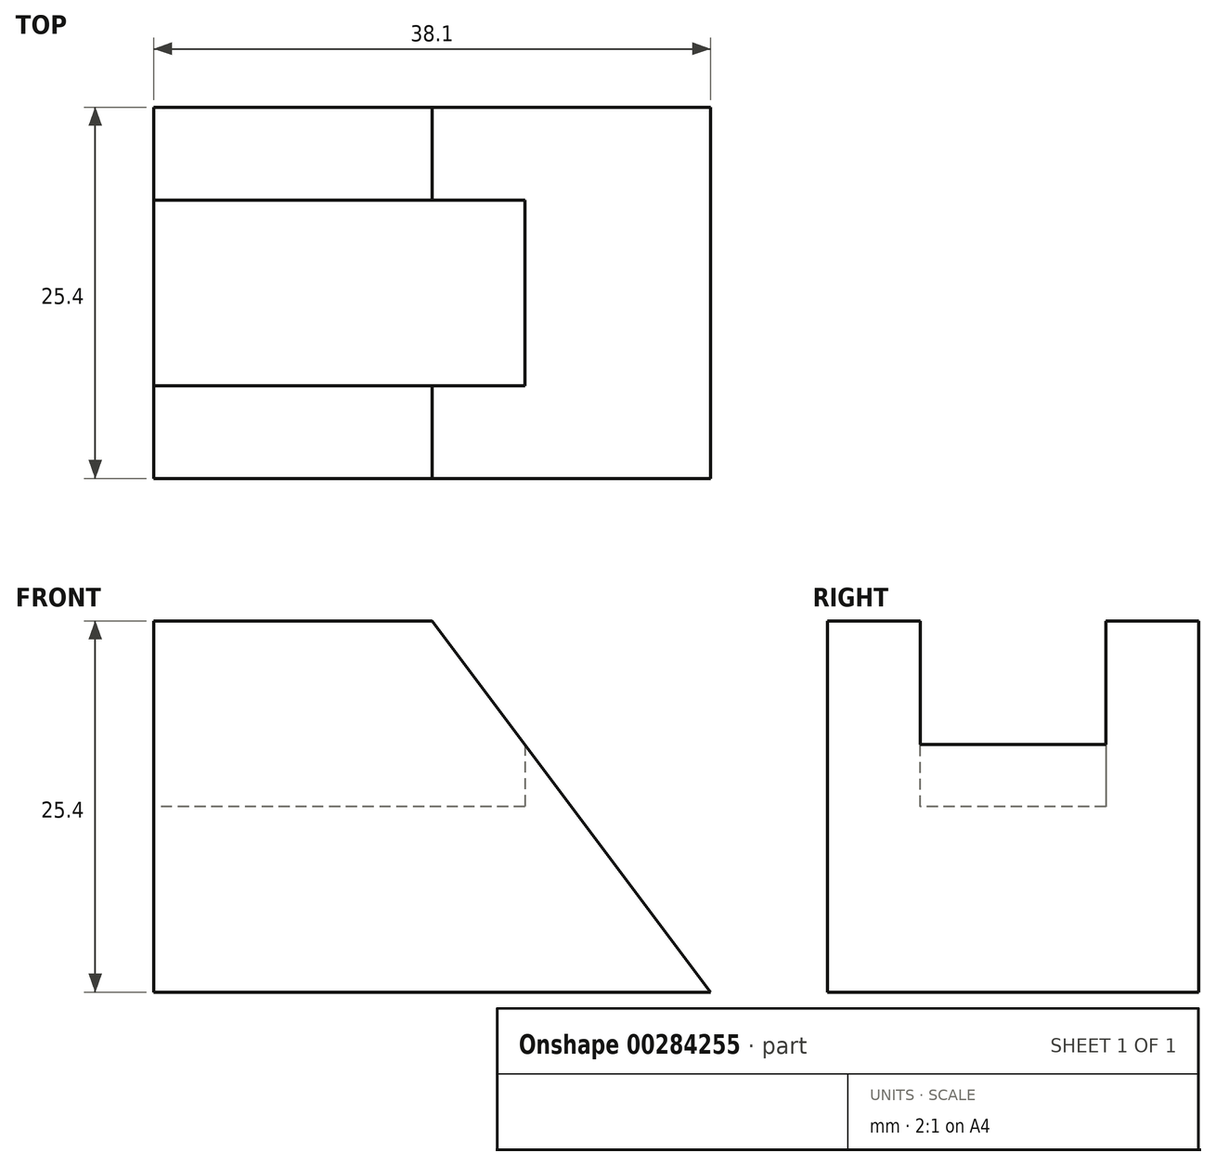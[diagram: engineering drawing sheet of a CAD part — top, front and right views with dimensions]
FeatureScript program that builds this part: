
annotation { "Feature Type Name" : "Feature", "Feature Type Description" : "" }
export const myFeature = defineFeature(function(context is Context, id is Id, definition is map)
    precondition{}
    {
        {
            var Q0;
            Q0=qCreatedBy(makeId("Front.planeOp"),FACE);
            var sketch = newSketch(context, id + "F0", { "sketchPlane" : qUnion([Q0])});
            skLineSegment(sketch, "E0", {"start": v(0, 0) * mm, "end": v(0, 25.4) * mm});
            skLineSegment(sketch, "E1", {"start": v(0, 25.4) * mm, "end": v(19.05, 25.4) * mm});
            skLineSegment(sketch, "E2", {"start": v(19.05, 25.4) * mm, "end": v(38.1, 0) * mm});
            skLineSegment(sketch, "E3", {"start": v(38.1, 0) * mm, "end": v(0, 0) * mm});
            skSolve(sketch);
        }
        {
            var Q0;
            Q0 = qSketchRegion(id + "F0", true);
            extrude(context, id + "F1", {"entities" : qUnion([Q0]), "depth" : 25.4 * mm});
        }
        {
            var Q0;
            Q0=makeQuery(id+"F1.opExtrude","SWEPT_FACE",FACE,{"disambiguationData":[OSD([sQuery(id+"F0.wireOp",EDGE,"E0")])]});
            var sketch = newSketch(context, id + "F2", { "sketchPlane" : qUnion([Q0])});
            skLineSegment(sketch, "E4", {"start": v(6.35, 25.4) * mm, "end": v(6.35, 12.7) * mm});
            skLineSegment(sketch, "E5", {"start": v(6.35, 12.7) * mm, "end": v(19.05, 12.7) * mm});
            skLineSegment(sketch, "E6", {"start": v(19.05, 12.7) * mm, "end": v(19.05, 25.4) * mm});
            skLineSegment(sketch, "E7", {"start": v(19.05, 25.4) * mm, "end": v(6.35, 25.4) * mm});
            skSolve(sketch);
        }
        {
            var Q0;
            Q0=makeQuery(id+"F2.imprint","IMPRINT",FACE,{"disambiguationData":[TD([[makeQuery(id+"F2.imprint","IMPRINT",EDGE,{"derivedFrom":sQuery(id+"F2.wireOp",EDGE,"E4")}),1.0]])]});
            extrude(context, id + "F3", {"entities" : qUnion([Q0]), "operationType" : NewBodyOperationType.REMOVE, "oppositeDirection" : true, "depth" : 25.4 * mm});
        }
    });
